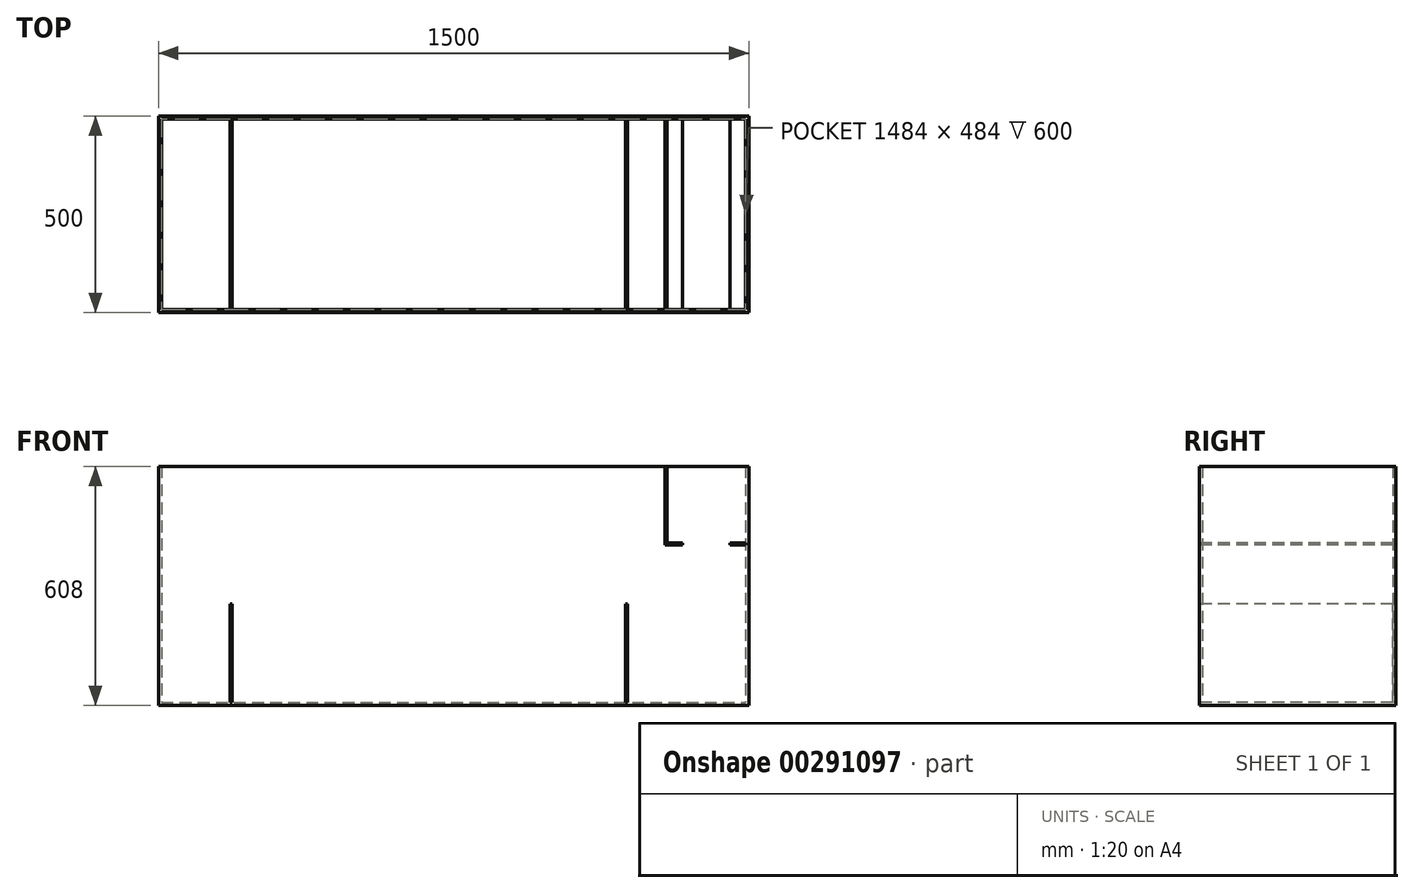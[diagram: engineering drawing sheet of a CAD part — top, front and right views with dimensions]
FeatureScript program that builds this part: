
annotation { "Feature Type Name" : "Feature", "Feature Type Description" : "" }
export const myFeature = defineFeature(function(context is Context, id is Id, definition is map)
    precondition{}
    {
        {
            var Q0;
            Q0=qCreatedBy(makeId("Top.planeOp"),FACE);
            var sketch = newSketch(context, id + "F0", { "sketchPlane" : qUnion([Q0])});
            skLineSegment(sketch, "E0.bottom", {"start": v(-750, 250) * mm, "end": v(750, 250) * mm});
            skLineSegment(sketch, "E0.top", {"start": v(-750, -250) * mm, "end": v(750, -250) * mm});
            skLineSegment(sketch, "E0.left", {"start": v(-750, 250) * mm, "end": v(-750, -250) * mm});
            skLineSegment(sketch, "E0.right", {"start": v(750, 250) * mm, "end": v(750, -250) * mm});
            skPoint(sketch, "E0.middle", {"position": v(0, 0) * mm});
            skLineSegment(sketch, "E1.bottom", {"start": v(-742, 242) * mm, "end": v(742, 242) * mm});
            skLineSegment(sketch, "E1.top", {"start": v(-742, -242) * mm, "end": v(742, -242) * mm});
            skLineSegment(sketch, "E1.left", {"start": v(-742, 242) * mm, "end": v(-742, -242) * mm});
            skLineSegment(sketch, "E1.right", {"start": v(742, 242) * mm, "end": v(742, -242) * mm});
            skSolve(sketch);
        }
        {
            var Q0;
            Q0=qSketchRegion(id+"F0",true);
            var Q1;
            Q1=makeQuery(id+"F0.imprint","IMPRINT",FACE,{"disambiguationData":[TD([[makeQuery(id+"F0.imprint","IMPRINT",EDGE,{"derivedFrom":sQuery(id+"F0.wireOp",EDGE,"E1.bottom")}),-1.0]])]});
            extrude(context, id + "F1", {"entities" : qUnion([Q0, Q1]), "oppositeDirection" : true, "depth" : 8 * mm});
        }
        {
            var Q0;
            Q0=qSketchRegion(id+"F0",true);
            extrude(context, id + "F2", {"entities" : qUnion([Q0]), "depth" : 600 * mm});
        }
        {
            var Q0;
            Q0=makeQuery(id+"F1.opExtrude","SWEPT_BODY",BODY,{"disambiguationData":[OSD([sQuery(id+"F0.wireOp",EDGE,"E0.bottom"),sQuery(id+"F0.wireOp",EDGE,"E0.top"),sQuery(id+"F0.wireOp",EDGE,"E0.left"),sQuery(id+"F0.wireOp",EDGE,"E0.right")])]});
            var Q1;
            Q1=makeQuery(id+"F2.opExtrude","SWEPT_BODY",BODY,{"disambiguationData":[OSD([sQuery(id+"F0.wireOp",EDGE,"E0.bottom"),sQuery(id+"F0.wireOp",EDGE,"E0.top"),sQuery(id+"F0.wireOp",EDGE,"E0.left"),sQuery(id+"F0.wireOp",EDGE,"E0.right"),sQuery(id+"F0.wireOp",EDGE,"E1.bottom"),sQuery(id+"F0.wireOp",EDGE,"E1.top"),sQuery(id+"F0.wireOp",EDGE,"E1.left"),sQuery(id+"F0.wireOp",EDGE,"E1.right")])]});
            booleanBodies(context, id + "F3", {"operationType" : BooleanOperationType.UNION, "tools" : qUnion([Q0, Q1])});
        }
        {
            var Q0;
            {var subQ0=sQuery(id+"F0.wireOp",EDGE,"E0.top");Q0=makeQuery(id+"F3.opBoolean","MERGE",FACE,{"derivedFrom":[makeQuery(id+"F1.opExtrude","SWEPT_FACE",FACE,{"disambiguationData":[OSD([subQ0])]}),makeQuery(id+"F2.opExtrude","SWEPT_FACE",FACE,{"disambiguationData":[OSD([subQ0])]})]});}
            var sketch = newSketch(context, id + "F4", { "sketchPlane" : qUnion([Q0])});
            skLineSegment(sketch, "E2", {"start": v(0, 0) * mm, "end": v(0, 341.46) * mm, "construction": true});
            skLineSegment(sketch, "E3.bottom", {"start": v(542, 600) * mm, "end": v(537, 600) * mm});
            skLineSegment(sketch, "E3.top", {"start": v(542, 400) * mm, "end": v(537, 400) * mm});
            skLineSegment(sketch, "E3.left", {"start": v(542, 600) * mm, "end": v(542, 400) * mm});
            skLineSegment(sketch, "E3.right", {"start": v(537, 600) * mm, "end": v(537, 400) * mm});
            skLineSegment(sketch, "E4.bottom", {"start": v(537, 400) * mm, "end": v(582, 400) * mm});
            skLineSegment(sketch, "E4.top", {"start": v(537, 405) * mm, "end": v(582, 405) * mm});
            skLineSegment(sketch, "E4.left", {"start": v(537, 400) * mm, "end": v(537, 405) * mm});
            skLineSegment(sketch, "E4.right", {"start": v(742.01, 400) * mm, "end": v(742.01, 405) * mm});
            skLineSegment(sketch, "E5", {"start": v(582, 405) * mm, "end": v(582, 400) * mm});
            skLineSegment(sketch, "E6", {"start": v(702.01, 405) * mm, "end": v(702.01, 400) * mm});
            skLineSegment(sketch, "E7.trimOffspring", {"start": v(702.01, 405) * mm, "end": v(742.01, 405) * mm});
            skLineSegment(sketch, "E8.trimOffspring", {"start": v(702.01, 400) * mm, "end": v(742.01, 400) * mm});
            skLineSegment(sketch, "E9.bottom", {"start": v(442, 0) * mm, "end": v(437, 0) * mm});
            skLineSegment(sketch, "E9.top", {"start": v(442, 250) * mm, "end": v(437, 250) * mm});
            skLineSegment(sketch, "E9.left", {"start": v(442, 0) * mm, "end": v(442, 250) * mm});
            skLineSegment(sketch, "E9.right", {"start": v(437, 0) * mm, "end": v(437, 250) * mm});
            skLineSegment(sketch, "E10.bottom", {"start": v(-563, 0) * mm, "end": v(-568, 0) * mm});
            skLineSegment(sketch, "E10.top", {"start": v(-563, 250) * mm, "end": v(-568, 250) * mm});
            skLineSegment(sketch, "E10.left", {"start": v(-563, 0) * mm, "end": v(-563, 250) * mm});
            skLineSegment(sketch, "E10.right", {"start": v(-568, 0) * mm, "end": v(-568, 250) * mm});
            skSolve(sketch);
        }
        {
            var Q0;
            Q0=qSketchRegion(id+"F4",true);
            var Q1;
            Q1=makeQuery(id+"F2.opExtrude","SWEPT_FACE",FACE,{"disambiguationData":[OSD([sQuery(id+"F0.wireOp",EDGE,"E1.bottom")])]});
            extrude(context, id + "F5", {"entities" : qUnion([Q0]), "endBound" : BoundingType.UP_TO_SURFACE, "oppositeDirection" : true, "endBoundEntityFace" : qUnion([Q1]), "depth" : 25 * mm});
        }
    });
